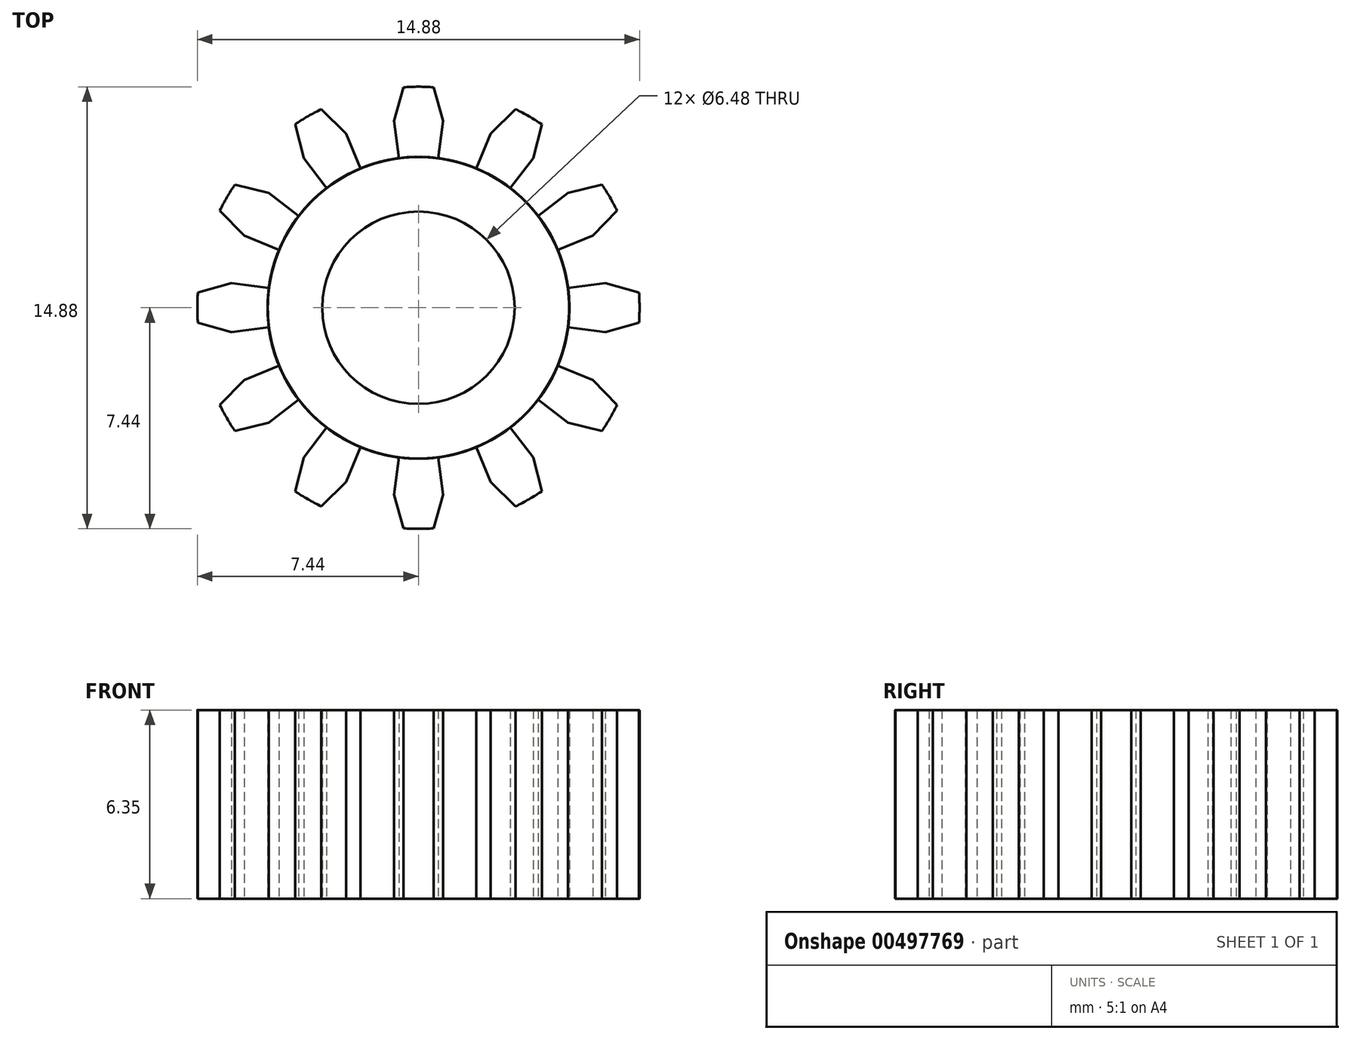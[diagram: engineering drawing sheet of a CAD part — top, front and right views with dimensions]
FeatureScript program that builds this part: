
annotation { "Feature Type Name" : "Feature", "Feature Type Description" : "" }
export const myFeature = defineFeature(function(context is Context, id is Id, definition is map)
    precondition{}
    {
        {
            var Q0;
            Q0=qCreatedBy(makeId("Top.planeOp"),FACE);
            var sketch = newSketch(context, id + "F0", { "sketchPlane" : qUnion([Q0])});
            skCircle(sketch, "E0", {"center": v(0, 0) * mm, "radius": 7.4 * mm, "construction": true});
            skCircle(sketch, "E1", {"center": v(0, 0) * mm, "radius": 3.24 * mm});
            skLineSegment(sketch, "E2", {"start": v(0, 3.24) * mm, "end": v(0, 7.4) * mm, "construction": true});
            skLineSegment(sketch, "E3", {"start": v(0.91, 5) * mm, "end": v(0.91, 5) * mm});
            skCircle(sketch, "E4.converted", {"center": v(0, 0) * mm, "radius": 5.08 * mm});
            skSolve(sketch);
        }
        {
            var Q0;
            Q0 = qSketchRegion(id + "F0", true);
            extrude(context, id + "F1", {"entities" : qUnion([Q0]), "depth" : 6.35 * mm});
        }
        {
            var Q0;
            Q0=qCreatedBy(makeId("Top.planeOp"),FACE);
            var sketch = newSketch(context, id + "F2", { "sketchPlane" : qUnion([Q0])});
            skLineSegment(sketch, "E5", {"start": v(-0.57, 4.36) * mm, "end": v(-0.83, 6.3) * mm});
            skLineSegment(sketch, "E6", {"start": v(0.57, 4.36) * mm, "end": v(0.83, 6.3) * mm});
            skArc(sketch, "E7", {"start": v(0.5, 7.42) * mm, "mid": v(0, 7.44) * mm, "end": v(-0.5, 7.42) * mm});
            skLineSegment(sketch, "E8", {"start": v(0, 7.44) * mm, "end": v(0, 0) * mm, "construction": true});
            skLineSegment(sketch, "E9", {"start": v(-0.5, 7.42) * mm, "end": v(-0.83, 6.3) * mm});
            skLineSegment(sketch, "E10", {"start": v(0.5, 7.42) * mm, "end": v(0.83, 6.3) * mm});
            skArc(sketch, "E11", {"start": v(0.5, 7.42) * mm, "mid": v(0, 7.44) * mm, "end": v(-0.5, 7.42) * mm, "construction": true});
            skCircle(sketch, "E12", {"center": v(0, 0) * mm, "radius": 6.35 * mm, "construction": true});
            skArc(sketch, "E13", {"start": v(0.57, 4.36) * mm, "mid": v(0, 4.4) * mm, "end": v(-0.57, 4.36) * mm});
            skSolve(sketch);
        }
        {
            var Q0;
            Q0 = qSketchRegion(id + "F2", true);
            extrude(context, id + "F3", {"entities" : qUnion([Q0]), "operationType" : NewBodyOperationType.ADD, "depth" : 6.35 * mm});
        }
        {
            var Q0;
            Q0=makeQuery(id+"F1.opExtrude","SWEPT_BODY",BODY,{"disambiguationData":[OSD([sQuery(id+"F0.wireOp",EDGE,"E1"),sQuery(id+"F0.wireOp",EDGE,"E4.converted")])]});
            var Q1;
            Q1=makeQuery(id+"F1.opExtrude","CAP_EDGE",EDGE,{"disambiguationData":[OSD([sQuery(id+"F0.wireOp",EDGE,"E1")])],"isStart":false});
            circularPattern(context, id + "F4", {"entities" : qUnion([Q0]), "axis" : qUnion([Q1]), "angle" : 360 * degree, "instanceCount" : 12, "equalSpace" : true});
        }
    });
